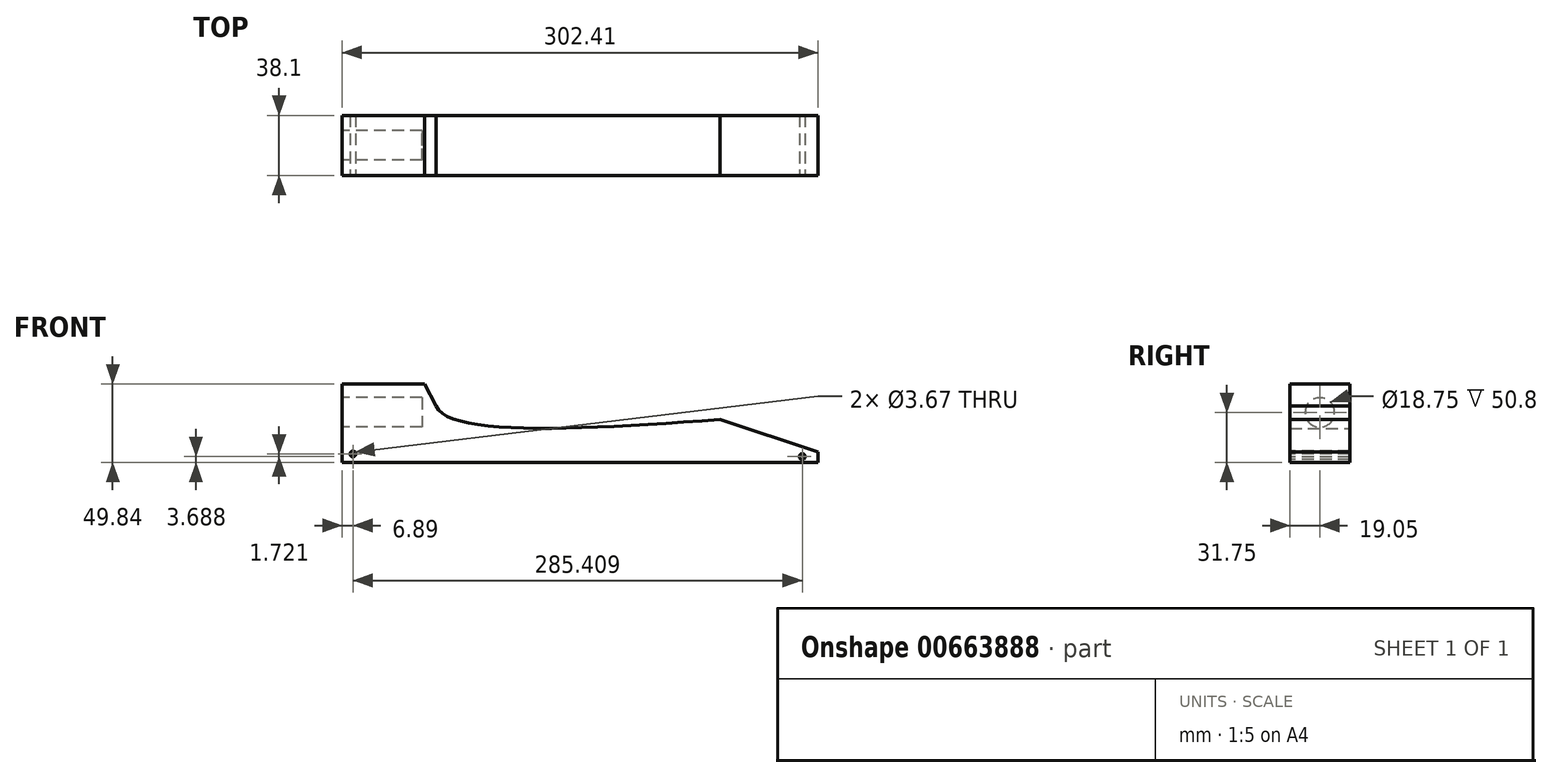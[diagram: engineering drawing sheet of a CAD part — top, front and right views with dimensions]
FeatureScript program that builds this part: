
annotation { "Feature Type Name" : "Feature", "Feature Type Description" : "" }
export const myFeature = defineFeature(function(context is Context, id is Id, definition is map)
    precondition{}
    {
        {
            var Q0;
            Q0=qCreatedBy(makeId("Front.planeOp"),FACE);
            var sketch = newSketch(context, id + "F0", { "sketchPlane" : qUnion([Q0])});
            skLineSegment(sketch, "E0", {"start": v(0, 0) * mm, "end": v(0, 63.5) * mm});
            skLineSegment(sketch, "E1", {"start": v(0, 63.5) * mm, "end": v(302.4, 25.4) * mm});
            skLineSegment(sketch, "E2", {"start": v(302.4, 25.4) * mm, "end": v(302.4, 0) * mm});
            skLineSegment(sketch, "E3", {"start": v(302.4, 0) * mm, "end": v(0, 0) * mm});
            skSolve(sketch);
        }
        {
            var Q0;
            Q0=makeQuery(id+"F0.imprint","IMPRINT",FACE,{"disambiguationData":[TD([[makeQuery(id+"F0.imprint","IMPRINT",EDGE,{"derivedFrom":sQuery(id+"F0.wireOp",EDGE,"E0")}),-1.0]])]});
            extrude(context, id + "F1", {"entities" : qUnion([Q0]), "depth" : 38.1 * mm, "offsetDistance" : 25.4 * mm});
        }
        {
            var Q0;
            Q0=makeQuery(id+"F1.opExtrude","SWEPT_FACE",FACE,{"disambiguationData":[OSD([sQuery(id+"F0.wireOp",EDGE,"E0")])]});
            var sketch = newSketch(context, id + "F2", { "sketchPlane" : qUnion([Q0])});
            skCircle(sketch, "E4", {"center": v(19.05, 31.75) * mm, "radius": 9.38 * mm});
            skPoint(sketch, "E4.centerSnap0", {"position": v(38.1, 31.75) * mm});
            skPoint(sketch, "E4.centerSnap1", {"position": v(19.05, 0) * mm});
            skSolve(sketch);
        }
        {
            var Q0;
            Q0=makeQuery(id+"F2.imprint","IMPRINT",FACE,{"disambiguationData":[TD([[makeQuery(id+"F2.imprint","IMPRINT",EDGE,{"derivedFrom":sQuery(id+"F2.wireOp",EDGE,"E4")}),1.0]])]});
            extrude(context, id + "F3", {"entities" : qUnion([Q0]), "operationType" : NewBodyOperationType.REMOVE, "oppositeDirection" : true, "depth" : 50.8 * mm, "offsetDistance" : 25.4 * mm});
        }
        {
            var Q0;
            Q0=makeQuery(id+"F1.opExtrude","CAP_FACE",FACE,{"disambiguationData":[OSD([sQuery(id+"F0.wireOp",EDGE,"E0"),sQuery(id+"F0.wireOp",EDGE,"E1"),sQuery(id+"F0.wireOp",EDGE,"E2"),sQuery(id+"F0.wireOp",EDGE,"E3")])],"isStart":false});
            var sketch = newSketch(context, id + "F4", { "sketchPlane" : qUnion([Q0])});
            skFitSpline(sketch, "E5", {"points": [v(61.55, 55.75) * mm, v(62.07, 32.58) * mm, v(269.36, 29.56) * mm], "startDerivative": vector(-32.29, -103.53) * mm, "endDerivative": vector(379.44, 29.1) * mm});
            skSolve(sketch);
        }
        {
            var Q0;
            {var subQ0=sQuery(id+"F4.wireOp",EDGE,"E5");Q0=makeQuery(id+"F4.imprint","IMPRINT",FACE,{"disambiguationData":[TD([[makeQuery(id+"F4.imprint","IMPRINT",EDGE,{"derivedFrom":subQ0}),1.0]])]});}
            extrude(context, id + "F5", {"entities" : qUnion([Q0]), "operationType" : NewBodyOperationType.REMOVE, "oppositeDirection" : true, "depth" : 76.2 * mm, "offsetDistance" : 25.4 * mm});
        }
        {
            var Q0;
            Q0=makeQuery(id+"F1.opExtrude","CAP_FACE",FACE,{"disambiguationData":[OSD([sQuery(id+"F0.wireOp",EDGE,"E0"),sQuery(id+"F0.wireOp",EDGE,"E1"),sQuery(id+"F0.wireOp",EDGE,"E2"),sQuery(id+"F0.wireOp",EDGE,"E3")])],"isStart":false});
            var sketch = newSketch(context, id + "F6", { "sketchPlane" : qUnion([Q0])});
            skLineSegment(sketch, "E6", {"start": v(0, 49.84) * mm, "end": v(59.8, 49.84) * mm});
            skLineSegment(sketch, "E7", {"start": v(59.8, 49.84) * mm, "end": v(61.55, 55.75) * mm});
            skLineSegment(sketch, "E8", {"start": v(61.55, 55.75) * mm, "end": v(0, 63.5) * mm});
            skLineSegment(sketch, "E9", {"start": v(0, 63.5) * mm, "end": v(0, 49.84) * mm});
            skSolve(sketch);
        }
        {
            var Q0;
            {var subQ0=sQuery(id+"F6.wireOp",EDGE,"E6");Q0=makeQuery(id+"F6.imprint","IMPRINT",FACE,{"disambiguationData":[TD([[makeQuery(id+"F6.imprint","IMPRINT",EDGE,{"derivedFrom":subQ0}),1.0]])]});}
            extrude(context, id + "F7", {"entities" : qUnion([Q0]), "operationType" : NewBodyOperationType.REMOVE, "oppositeDirection" : true, "depth" : 76.2 * mm, "offsetDistance" : 25.4 * mm});
        }
        {
            var Q0;
            Q0=makeQuery(id+"F1.opExtrude","CAP_FACE",FACE,{"disambiguationData":[OSD([sQuery(id+"F0.wireOp",EDGE,"E0"),sQuery(id+"F0.wireOp",EDGE,"E1"),sQuery(id+"F0.wireOp",EDGE,"E2"),sQuery(id+"F0.wireOp",EDGE,"E3")])],"isStart":false});
            var sketch = newSketch(context, id + "F8", { "sketchPlane" : qUnion([Q0])});
            skLineSegment(sketch, "E10", {"start": v(52.55, 49.84) * mm, "end": v(59.8, 35.72) * mm});
            skSolve(sketch);
        }
        {
            var Q0;
            {var subQ0=sQuery(id+"F8.wireOp",EDGE,"E10");Q0=makeQuery(id+"F8.imprint","IMPRINT",FACE,{"disambiguationData":[TD([[makeQuery(id+"F8.imprint","IMPRINT",EDGE,{"derivedFrom":subQ0}),1.0]])]});}
            extrude(context, id + "F9", {"entities" : qUnion([Q0]), "operationType" : NewBodyOperationType.REMOVE, "oppositeDirection" : true, "depth" : 76.2 * mm, "offsetDistance" : 25.4 * mm});
        }
        {
            var Q0;
            Q0=makeQuery(id+"F1.opExtrude","CAP_FACE",FACE,{"disambiguationData":[OSD([sQuery(id+"F0.wireOp",EDGE,"E0"),sQuery(id+"F0.wireOp",EDGE,"E1"),sQuery(id+"F0.wireOp",EDGE,"E2"),sQuery(id+"F0.wireOp",EDGE,"E3")])],"isStart":false});
            var sketch = newSketch(context, id + "F10", { "sketchPlane" : qUnion([Q0])});
            skLineSegment(sketch, "E11", {"start": v(269.36, 29.56) * mm, "end": v(302.4, 6.54) * mm});
            skSolve(sketch);
        }
        {
            var Q0;
            {var subQ0=sQuery(id+"F10.wireOp",EDGE,"E11");Q0=makeQuery(id+"F10.imprint","IMPRINT",FACE,{"disambiguationData":[TD([[makeQuery(id+"F10.imprint","IMPRINT",EDGE,{"derivedFrom":subQ0}),1.0]])]});}
            extrude(context, id + "F11", {"entities" : qUnion([Q0]), "operationType" : NewBodyOperationType.REMOVE, "oppositeDirection" : true, "depth" : 76.2 * mm, "offsetDistance" : 25.4 * mm});
        }
        {
            var Q0;
            Q0=makeQuery(id+"F1.opExtrude","CAP_FACE",FACE,{"disambiguationData":[OSD([sQuery(id+"F0.wireOp",EDGE,"E0"),sQuery(id+"F0.wireOp",EDGE,"E1"),sQuery(id+"F0.wireOp",EDGE,"E2"),sQuery(id+"F0.wireOp",EDGE,"E3")])],"isStart":false});
            var sketch = newSketch(context, id + "F12", { "sketchPlane" : qUnion([Q0])});
            skLineSegment(sketch, "E12", {"start": v(240.16, 27.35) * mm, "end": v(302.4, 6.54) * mm});
            skSolve(sketch);
        }
        {
            var Q0;
            {var subQ0=sQuery(id+"F12.wireOp",EDGE,"E12");Q0=makeQuery(id+"F12.imprint","IMPRINT",FACE,{"disambiguationData":[TD([[makeQuery(id+"F12.imprint","IMPRINT",EDGE,{"derivedFrom":subQ0}),1.0]])]});}
            extrude(context, id + "F13", {"entities" : qUnion([Q0]), "operationType" : NewBodyOperationType.REMOVE, "oppositeDirection" : true, "depth" : 76.2 * mm, "offsetDistance" : 25.4 * mm});
        }
        {
            var Q0;
            Q0=makeQuery(id+"F1.opExtrude","CAP_FACE",FACE,{"disambiguationData":[OSD([sQuery(id+"F0.wireOp",EDGE,"E0"),sQuery(id+"F0.wireOp",EDGE,"E1"),sQuery(id+"F0.wireOp",EDGE,"E2"),sQuery(id+"F0.wireOp",EDGE,"E3")])],"isStart":false});
            var sketch = newSketch(context, id + "F14", { "sketchPlane" : qUnion([Q0])});
            skCircle(sketch, "E13", {"center": v(6.89, 5.4) * mm, "radius": 1.84 * mm});
            skSolve(sketch);
        }
        {
            var Q0;
            Q0=makeQuery(id+"F14.imprint","IMPRINT",FACE,{"disambiguationData":[TD([[makeQuery(id+"F14.imprint","IMPRINT",EDGE,{"derivedFrom":sQuery(id+"F14.wireOp",EDGE,"E13")}),-1.0]])]});
            var sketch = newSketch(context, id + "F15", { "sketchPlane" : qUnion([Q0])});
            skCircle(sketch, "E14", {"center": v(292.3, 3.69) * mm, "radius": 1.84 * mm});
            skSolve(sketch);
        }
        {
            var Q0;
            Q0=makeQuery(id+"F14.imprint","IMPRINT",FACE,{"disambiguationData":[TD([[makeQuery(id+"F14.imprint","IMPRINT",EDGE,{"derivedFrom":sQuery(id+"F14.wireOp",EDGE,"E13")}),1.0]])]});
            extrude(context, id + "F16", {"entities" : qUnion([Q0]), "operationType" : NewBodyOperationType.REMOVE, "oppositeDirection" : true, "depth" : 76.2 * mm, "offsetDistance" : 25.4 * mm});
        }
        {
            var Q0;
            Q0=makeQuery(id+"F15.imprint","IMPRINT",FACE,{"disambiguationData":[TD([[makeQuery(id+"F15.imprint","IMPRINT",EDGE,{"derivedFrom":sQuery(id+"F15.wireOp",EDGE,"E14")}),1.0]])]});
            extrude(context, id + "F17", {"entities" : qUnion([Q0]), "operationType" : NewBodyOperationType.REMOVE, "oppositeDirection" : true, "depth" : 76.2 * mm, "offsetDistance" : 25.4 * mm});
        }
    });
